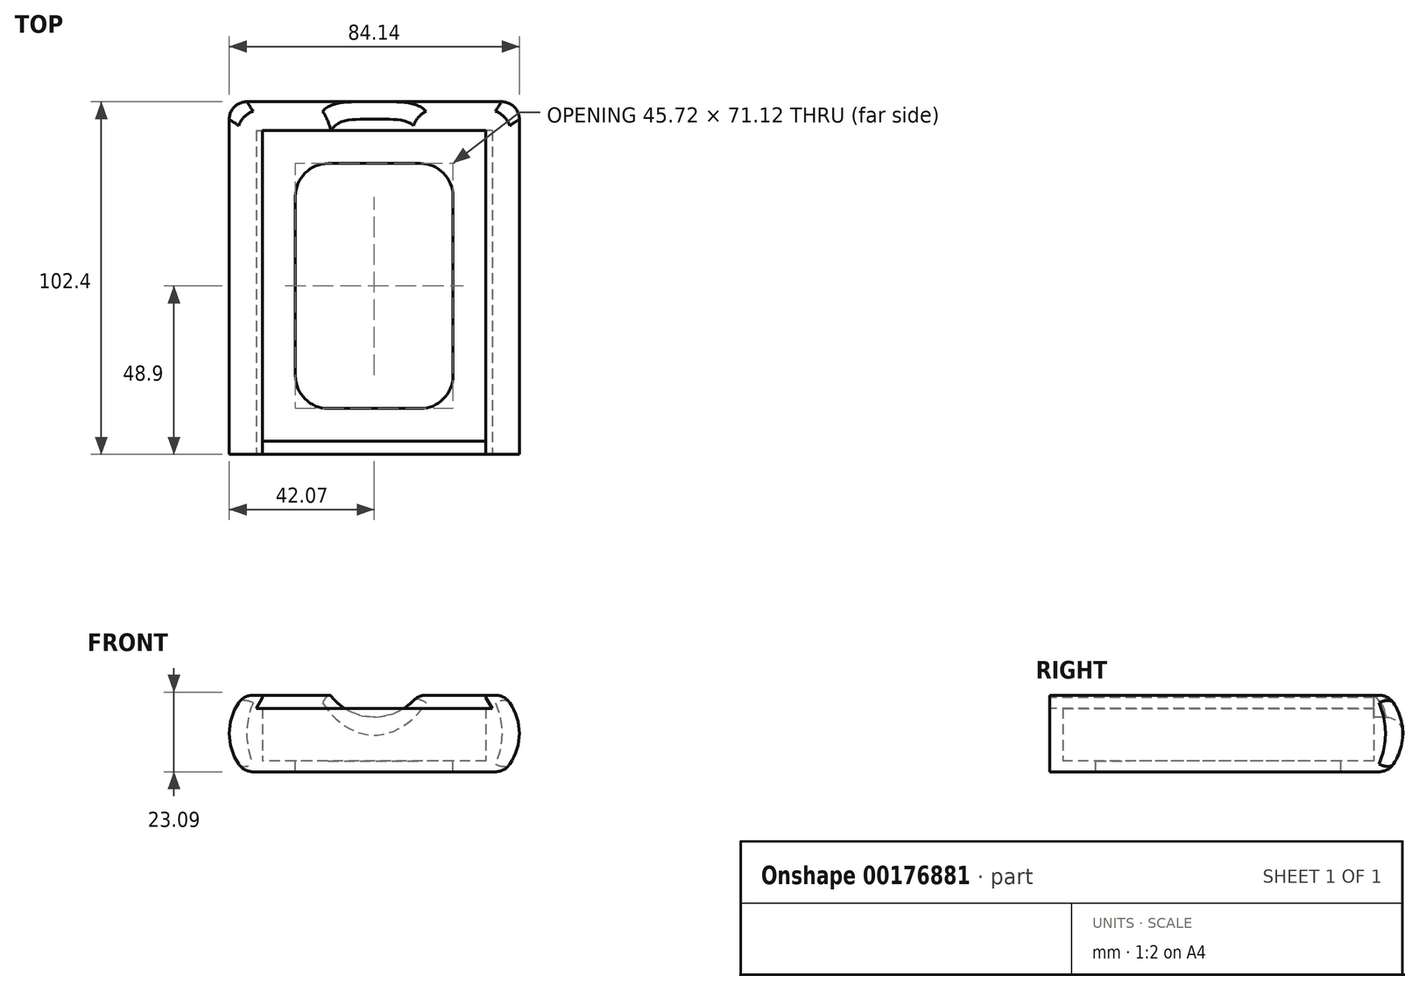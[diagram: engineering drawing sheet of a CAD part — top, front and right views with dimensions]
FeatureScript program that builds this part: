
annotation { "Feature Type Name" : "Feature", "Feature Type Description" : "" }
export const myFeature = defineFeature(function(context is Context, id is Id, definition is map)
    precondition{}
    {
        {
            var Q0;
            Q0=qCreatedBy(makeId("Top.planeOp"),FACE);
            var sketch = newSketch(context, id + "F0", { "sketchPlane" : qUnion([Q0])});
            skLineSegment(sketch, "E0.bottom", {"start": v(32.39, 45.09) * mm, "end": v(-32.39, 45.09) * mm, "construction": true});
            skLineSegment(sketch, "E0.top", {"start": v(32.39, -45.09) * mm, "end": v(-32.39, -45.09) * mm, "construction": true});
            skLineSegment(sketch, "E0.left", {"start": v(32.39, 45.09) * mm, "end": v(32.39, -45.09) * mm, "construction": true});
            skLineSegment(sketch, "E0.right", {"start": v(-32.39, 45.09) * mm, "end": v(-32.39, -45.09) * mm, "construction": true});
            skPoint(sketch, "E0.middle", {"position": v(0, 0) * mm});
            skLineSegment(sketch, "E1.bottom", {"start": v(37.47, 48.9) * mm, "end": v(-37.47, 48.9) * mm});
            skLineSegment(sketch, "E1.top", {"start": v(37.47, -48.9) * mm, "end": v(-37.47, -48.9) * mm});
            skLineSegment(sketch, "E1.left", {"start": v(37.47, 48.9) * mm, "end": v(37.47, -48.9) * mm});
            skLineSegment(sketch, "E1.right", {"start": v(-37.47, 48.9) * mm, "end": v(-37.47, -48.9) * mm});
            skSolve(sketch);
        }
        {
            var Q0;
            Q0 = qSketchRegion(id + "F0", true);
            var Q1;
            Q1=sQuery(id+"F0.wireOp",EDGE,"E0.bottom");
            var Q2;
            Q2=sQuery(id+"F0.wireOp",EDGE,"E0.right");
            var Q3;
            Q3=sQuery(id+"F0.wireOp",EDGE,"E0.top");
            var Q4;
            Q4=sQuery(id+"F0.wireOp",EDGE,"E0.left");
            extrude(context, id + "F1", {"entities" : qUnion([Q0]), "surfaceEntities" : qUnion([Q1, Q2, Q3, Q4]), "depth" : 3.17 * mm});
        }
        {
            var Q0;
            Q0=makeQuery(id+"F1.opExtrude","CAP_FACE",FACE,{"disambiguationData":[OSD([sQuery(id+"F0.wireOp",EDGE,"E1.bottom"),sQuery(id+"F0.wireOp",EDGE,"E1.top"),sQuery(id+"F0.wireOp",EDGE,"E1.left"),sQuery(id+"F0.wireOp",EDGE,"E1.right")])],"isStart":false});
            var sketch = newSketch(context, id + "F2", { "sketchPlane" : qUnion([Q0])});
            skLineSegment(sketch, "E2.bottom", {"start": v(-37.47, 48.9) * mm, "end": v(37.47, 48.9) * mm});
            skLineSegment(sketch, "E2.top", {"start": v(-37.47, -48.9) * mm, "end": v(37.47, -48.9) * mm});
            skLineSegment(sketch, "E2.left", {"start": v(-37.47, 48.9) * mm, "end": v(-37.47, -48.9) * mm});
            skLineSegment(sketch, "E2.right", {"start": v(37.47, 48.9) * mm, "end": v(37.47, -48.9) * mm});
            skLineSegment(sketch, "E3.bottom", {"start": v(32.38, 45.09) * mm, "end": v(-32.39, 45.09) * mm});
            skLineSegment(sketch, "E3.top", {"start": v(32.39, -45.09) * mm, "end": v(-32.38, -45.09) * mm});
            skLineSegment(sketch, "E3.left", {"start": v(32.38, 45.09) * mm, "end": v(32.39, -45.09) * mm});
            skLineSegment(sketch, "E3.right", {"start": v(-32.39, 45.09) * mm, "end": v(-32.38, -45.09) * mm});
            skPoint(sketch, "E3.middle", {"position": v(0, 0) * mm});
            skSolve(sketch);
        }
        {
            var Q0;
            Q0 = qSketchRegion(id + "F2", true);
            extrude(context, id + "F3", {"entities" : qUnion([Q0]), "operationType" : NewBodyOperationType.ADD, "depth" : 19.05 * mm});
        }
        {
            var Q0;
            Q0=makeQuery(id+"F3.boolean.opBoolean","MERGE",FACE,{"derivedFrom":[makeQuery(id+"F1.opExtrude","SWEPT_FACE",FACE,{"disambiguationData":[OSD([sQuery(id+"F0.wireOp",EDGE,"E1.top")])]}),makeQuery(id+"F3.opExtrude","SWEPT_FACE",FACE,{"disambiguationData":[OSD([sQuery(id+"F2.wireOp",EDGE,"E2.top")])]})]});
            var sketch = newSketch(context, id + "F4", { "sketchPlane" : qUnion([Q0])});
            skLineSegment(sketch, "E4", {"start": v(-32.38, 22.23) * mm, "end": v(-32.38, 21.59) * mm});
            skLineSegment(sketch, "E5", {"start": v(-32.38, 21.59) * mm, "end": v(-34.22, 18.41) * mm});
            skLineSegment(sketch, "E6", {"start": v(-34.22, 18.41) * mm, "end": v(0, 18.41) * mm});
            skLineSegment(sketch, "E7", {"start": v(0, 18.41) * mm, "end": v(0, 22.23) * mm, "construction": true});
            skLineSegment(sketch, "E8", {"start": v(0, 22.23) * mm, "end": v(-32.38, 22.23) * mm});
            skLineSegment(sketch, "E9.MirrorCS", {"start": v(0, 22.23) * mm, "end": v(32.38, 22.22) * mm});
            skLineSegment(sketch, "E10.MirrorCS", {"start": v(32.38, 22.23) * mm, "end": v(32.38, 21.59) * mm});
            skLineSegment(sketch, "E11.MirrorCS", {"start": v(32.38, 21.59) * mm, "end": v(34.22, 18.41) * mm});
            skLineSegment(sketch, "E12.MirrorCS", {"start": v(34.22, 18.42) * mm, "end": v(0, 18.41) * mm});
            skSolve(sketch);
        }
        {
            var Q0;
            Q0 = qSketchRegion(id + "F4", true);
            var Q1;
            Q1=makeQuery(id+"F3.opExtrude","SWEPT_FACE",FACE,{"disambiguationData":[OSD([sQuery(id+"F2.wireOp",EDGE,"E3.bottom")])]});
            extrude(context, id + "F5", {"entities" : qUnion([Q0]), "operationType" : NewBodyOperationType.REMOVE, "endBound" : BoundingType.UP_TO_SURFACE, "oppositeDirection" : true, "endBoundEntityFace" : qUnion([Q1]), "depth" : 25.4 * mm});
        }
        {
            var Q0;
            Q0=makeQuery(id+"F3.boolean.opBoolean","MERGE",FACE,{"derivedFrom":[makeQuery(id+"F1.opExtrude","SWEPT_FACE",FACE,{"disambiguationData":[OSD([sQuery(id+"F0.wireOp",EDGE,"E1.top")])]}),makeQuery(id+"F3.opExtrude","SWEPT_FACE",FACE,{"disambiguationData":[OSD([sQuery(id+"F2.wireOp",EDGE,"E2.top")])]})]});
            var sketch = newSketch(context, id + "F6", { "sketchPlane" : qUnion([Q0])});
            skArc(sketch, "E13", {"start": v(-37.47, 22.23) * mm, "mid": v(-42.07, 11.11) * mm, "end": v(-37.47, 0) * mm});
            skLineSegment(sketch, "E14", {"start": v(-37.46, 0) * mm, "end": v(-37.46, 22.23) * mm});
            skLineSegment(sketch, "E15", {"start": v(-37.47, 0) * mm, "end": v(-48.04, 10.57) * mm, "construction": true});
            skSolve(sketch);
        }
        {
            var Q0;
            Q0=qCreatedBy(makeId("Top.planeOp"),FACE);
            var sketch = newSketch(context, id + "F7", { "sketchPlane" : qUnion([Q0])});
            skLineSegment(sketch, "E16", {"start": v(-37.47, -48.9) * mm, "end": v(-37.47, 48.9) * mm});
            skLineSegment(sketch, "E17", {"start": v(-37.47, 48.9) * mm, "end": v(37.47, 48.9) * mm});
            skLineSegment(sketch, "E18", {"start": v(37.47, 48.9) * mm, "end": v(37.47, -48.9) * mm});
            skSolve(sketch);
        }
        {
            var Q0;
            Q0 = qSketchRegion(id + "F6", true);
            var Q1;
            Q1 = qConstructionFilter(qBodyType(qCreatedBy(id + "F7" ,EDGE), BodyType.WIRE), ConstructionObject.NO);
            sweep(context, id + "F8", {"operationType" : NewBodyOperationType.ADD, "profiles" : qUnion([Q0]), "path" : qUnion([Q1])});
        }
        {
            var Q0;
            {var subQ0=sQuery(id+"F2.wireOp",EDGE,"E3.bottom");Q0=makeQuery(id+"F5.boolean.opBoolean","MERGE",FACE,{"derivedFrom":[makeQuery(id+"F3.opExtrude","SWEPT_FACE",FACE,{"disambiguationData":[OSD([subQ0])]}),makeQuery(id+"F5.opExtrude","CAP_FACE",FACE,{"disambiguationData":[OSD([subQ0])],"isStart":false})]});}
            var sketch = newSketch(context, id + "F9", { "sketchPlane" : qUnion([Q0])});
            skArc(sketch, "E19", {"start": v(-12.7, 22.23) * mm, "mid": v(0, 15.87) * mm, "end": v(12.7, 22.23) * mm});
            skLineSegment(sketch, "E20", {"start": v(-12.7, 22.23) * mm, "end": v(0, 22.23) * mm});
            skLineSegment(sketch, "E21", {"start": v(0, 22.23) * mm, "end": v(12.7, 22.23) * mm});
            skLineSegment(sketch, "E22", {"start": v(0, 22.23) * mm, "end": v(0, 15.88) * mm, "construction": true});
            skSolve(sketch);
        }
        {
            var Q0;
            Q0 = qSketchRegion(id + "F9", true);
            extrude(context, id + "F10", {"entities" : qUnion([Q0]), "operationType" : NewBodyOperationType.REMOVE, "endBound" : BoundingType.THROUGH_ALL, "oppositeDirection" : true, "depth" : 25.4 * mm});
        }
        {
            var Q0;
            Q0=makeQuery(id+"F1.opExtrude","CAP_FACE",FACE,{"disambiguationData":[OSD([sQuery(id+"F0.wireOp",EDGE,"E1.bottom"),sQuery(id+"F0.wireOp",EDGE,"E1.top"),sQuery(id+"F0.wireOp",EDGE,"E1.left"),sQuery(id+"F0.wireOp",EDGE,"E1.right")])],"isStart":false});
            var sketch = newSketch(context, id + "F11", { "sketchPlane" : qUnion([Q0])});
            skLineSegment(sketch, "E23.bottom", {"start": v(-32.39, 45.09) * mm, "end": v(32.39, 45.09) * mm, "construction": true});
            skLineSegment(sketch, "E23.top", {"start": v(-32.39, -45.09) * mm, "end": v(32.39, -45.09) * mm, "construction": true});
            skLineSegment(sketch, "E23.left", {"start": v(-32.39, 45.09) * mm, "end": v(-32.39, -45.09) * mm, "construction": true});
            skLineSegment(sketch, "E23.right", {"start": v(32.39, 45.09) * mm, "end": v(32.39, -45.09) * mm, "construction": true});
            skLineSegment(sketch, "E24.bottom", {"start": v(-22.86, 35.56) * mm, "end": v(22.86, 35.56) * mm});
            skLineSegment(sketch, "E24.top", {"start": v(-22.86, -35.56) * mm, "end": v(22.86, -35.56) * mm});
            skLineSegment(sketch, "E24.left", {"start": v(-22.86, 35.56) * mm, "end": v(-22.86, -35.56) * mm});
            skLineSegment(sketch, "E24.right", {"start": v(22.86, 35.56) * mm, "end": v(22.86, -35.56) * mm});
            skPoint(sketch, "E24.middle", {"position": v(0, 0) * mm});
            skSolve(sketch);
        }
        {
            var Q0;
            Q0 = qSketchRegion(id + "F11", true);
            extrude(context, id + "F12", {"entities" : qUnion([Q0]), "operationType" : NewBodyOperationType.REMOVE, "endBound" : BoundingType.THROUGH_ALL, "oppositeDirection" : true, "depth" : 25.4 * mm});
        }
        {
            var Q0;
            Q0=makeQuery(id+"F10.boolean.opBoolean","COPY",EDGE,{"derivedFrom":makeQuery(id+"F10.opExtrude","SWEPT_EDGE",EDGE,{"disambiguationData":[OSD([sQuery(id+"F2.wireOp",EDGE,"E3.bottom"),sQuery(id+"F9.wireOp",EDGE,"E19"),sQuery(id+"F9.wireOp",EDGE,"E20")])]})});
            var Q1;
            Q1=makeQuery(id+"F10.boolean.opBoolean","INTERSECT",EDGE,{"derivedFrom":[makeQuery(id+"F8.opSweep","SWEPT_FACE",FACE,{"disambiguationData":[OSD([sQuery(id+"F6.wireOp",EDGE,"E13"),sQuery(id+"F7.wireOp",EDGE,"E17")])]}),makeQuery(id+"F10.opExtrude","SWEPT_FACE",FACE,{"disambiguationData":[OSD([sQuery(id+"F9.wireOp",EDGE,"E19")])]})]});
            var Q2;
            Q2=makeQuery(id+"F10.boolean.opBoolean","COPY",EDGE,{"derivedFrom":makeQuery(id+"F10.opExtrude","SWEPT_EDGE",EDGE,{"disambiguationData":[OSD([sQuery(id+"F2.wireOp",EDGE,"E3.bottom"),sQuery(id+"F9.wireOp",EDGE,"E19"),sQuery(id+"F9.wireOp",EDGE,"E21")])]})});
            var Q3;
            Q3=makeQuery(id+"F8.opSweep","MID_CAP_EDGE",EDGE,{"disambiguationData":[OSD([sQuery(id+"F6.wireOp",EDGE,"E13"),sQuery(id+"F7.wireOp",VERTEX,"E18.start")])],"capPos":2.0});
            var Q4;
            Q4=makeQuery(id+"F8.opSweep","MID_CAP_EDGE",EDGE,{"disambiguationData":[OSD([sQuery(id+"F6.wireOp",EDGE,"E13"),sQuery(id+"F7.wireOp",VERTEX,"E17.start")])],"capPos":1.0});
            var Q5;
            Q5=makeQuery(id+"F8.boolean.opBoolean","MERGE",EDGE,{"derivedFrom":[makeQuery(id+"F3.opExtrude","CAP_EDGE",EDGE,{"disambiguationData":[OSD([sQuery(id+"F2.wireOp",EDGE,"E2.right")])],"isStart":false}),makeQuery(id+"F8.opSweep","SWEPT_EDGE",EDGE,{"disambiguationData":[OSD([sQuery(id+"F2.wireOp",EDGE,"E2.top"),sQuery(id+"F6.wireOp",EDGE,"E13"),sQuery(id+"F6.wireOp",EDGE,"E14"),sQuery(id+"F7.wireOp",EDGE,"E18")])]})]});
            var Q6;
            {var subQ0=sQuery(id+"F2.wireOp",EDGE,"E2.top");var subQ1=sQuery(id+"F2.wireOp",EDGE,"E2.bottom");var subQ2=sQuery(id+"F7.wireOp",EDGE,"E17");var subQ3=sQuery(id+"F6.wireOp",EDGE,"E13");Q6=makeQuery(id+"F10.boolean.opBoolean","SPLIT",EDGE,{"disambiguationData":[TD([makeQuery(id+"F8.opSweep","SWEPT_FACE",FACE,{"disambiguationData":[OSD([subQ3,sQuery(id+"F7.wireOp",EDGE,"E18")])]})])],"derivedFrom":makeQuery(id+"F8.boolean.opBoolean","MERGE",EDGE,{"derivedFrom":[makeQuery(id+"F3.opExtrude","CAP_EDGE",EDGE,{"disambiguationData":[OSD([subQ1])],"isStart":false}),makeQuery(id+"F8.opSweep","SWEPT_EDGE",EDGE,{"disambiguationData":[OSD([subQ0,subQ3,sQuery(id+"F6.wireOp",EDGE,"E14"),subQ2])]})]})});}
            var Q7;
            {var subQ0=sQuery(id+"F2.wireOp",EDGE,"E2.top");var subQ1=sQuery(id+"F2.wireOp",EDGE,"E2.bottom");var subQ2=sQuery(id+"F6.wireOp",EDGE,"E13");var subQ3=sQuery(id+"F7.wireOp",EDGE,"E17");Q7=makeQuery(id+"F10.boolean.opBoolean","SPLIT",EDGE,{"disambiguationData":[TD([makeQuery(id+"F8.opSweep","SWEPT_FACE",FACE,{"disambiguationData":[OSD([subQ2,sQuery(id+"F7.wireOp",EDGE,"E16")])]})])],"derivedFrom":makeQuery(id+"F8.boolean.opBoolean","MERGE",EDGE,{"derivedFrom":[makeQuery(id+"F3.opExtrude","CAP_EDGE",EDGE,{"disambiguationData":[OSD([subQ1])],"isStart":false}),makeQuery(id+"F8.opSweep","SWEPT_EDGE",EDGE,{"disambiguationData":[OSD([subQ0,subQ2,sQuery(id+"F6.wireOp",EDGE,"E14"),subQ3])]})]})});}
            var Q8;
            Q8=makeQuery(id+"F8.boolean.opBoolean","MERGE",EDGE,{"derivedFrom":[makeQuery(id+"F3.opExtrude","CAP_EDGE",EDGE,{"disambiguationData":[OSD([sQuery(id+"F2.wireOp",EDGE,"E2.left")])],"isStart":false}),makeQuery(id+"F8.opSweep","SWEPT_EDGE",EDGE,{"disambiguationData":[OSD([sQuery(id+"F2.wireOp",EDGE,"E2.top"),sQuery(id+"F6.wireOp",EDGE,"E13"),sQuery(id+"F6.wireOp",EDGE,"E14"),sQuery(id+"F7.wireOp",EDGE,"E16")])]})]});
            var Q9;
            Q9=makeQuery(id+"F8.boolean.opBoolean","MERGE",EDGE,{"derivedFrom":[makeQuery(id+"F1.opExtrude","CAP_EDGE",EDGE,{"disambiguationData":[OSD([sQuery(id+"F0.wireOp",EDGE,"E1.bottom")])],"isStart":true}),makeQuery(id+"F8.opSweep","SWEPT_EDGE",EDGE,{"disambiguationData":[OSD([sQuery(id+"F0.wireOp",EDGE,"E1.top"),sQuery(id+"F6.wireOp",EDGE,"E13"),sQuery(id+"F6.wireOp",EDGE,"E14"),sQuery(id+"F7.wireOp",EDGE,"E17")])]})]});
            var Q10;
            Q10=makeQuery(id+"F8.boolean.opBoolean","MERGE",EDGE,{"derivedFrom":[makeQuery(id+"F1.opExtrude","CAP_EDGE",EDGE,{"disambiguationData":[OSD([sQuery(id+"F0.wireOp",EDGE,"E1.right")])],"isStart":true}),makeQuery(id+"F8.opSweep","SWEPT_EDGE",EDGE,{"disambiguationData":[OSD([sQuery(id+"F0.wireOp",EDGE,"E1.top"),sQuery(id+"F6.wireOp",EDGE,"E13"),sQuery(id+"F6.wireOp",EDGE,"E14"),sQuery(id+"F7.wireOp",EDGE,"E16")])]})]});
            var Q11;
            Q11=makeQuery(id+"F8.boolean.opBoolean","MERGE",EDGE,{"derivedFrom":[makeQuery(id+"F1.opExtrude","CAP_EDGE",EDGE,{"disambiguationData":[OSD([sQuery(id+"F0.wireOp",EDGE,"E1.left")])],"isStart":true}),makeQuery(id+"F8.opSweep","SWEPT_EDGE",EDGE,{"disambiguationData":[OSD([sQuery(id+"F0.wireOp",EDGE,"E1.top"),sQuery(id+"F6.wireOp",EDGE,"E13"),sQuery(id+"F6.wireOp",EDGE,"E14"),sQuery(id+"F7.wireOp",EDGE,"E18")])]})]});
            fillet(context, id + "F13", {"entities" : qUnion([Q0, Q1, Q2, Q3, Q4, Q5, Q6, Q7, Q8, Q9, Q10, Q11]), "radius" : 5.08 * mm, "tangentPropagation" : true, "allowEdgeOverflow" : false});
        }
        {
            var Q0;
            Q0=makeQuery(id+"F12.boolean.opBoolean","COPY",EDGE,{"derivedFrom":makeQuery(id+"F12.opExtrude","SWEPT_EDGE",EDGE,{"disambiguationData":[OSD([sQuery(id+"F11.wireOp",EDGE,"E24.bottom"),sQuery(id+"F11.wireOp",EDGE,"E24.right")])]})});
            var Q1;
            Q1=makeQuery(id+"F12.boolean.opBoolean","COPY",EDGE,{"derivedFrom":makeQuery(id+"F12.opExtrude","SWEPT_EDGE",EDGE,{"disambiguationData":[OSD([sQuery(id+"F11.wireOp",EDGE,"E24.bottom"),sQuery(id+"F11.wireOp",EDGE,"E24.left")])]})});
            var Q2;
            Q2=makeQuery(id+"F12.boolean.opBoolean","COPY",EDGE,{"derivedFrom":makeQuery(id+"F12.opExtrude","SWEPT_EDGE",EDGE,{"disambiguationData":[OSD([sQuery(id+"F11.wireOp",EDGE,"E24.top"),sQuery(id+"F11.wireOp",EDGE,"E24.left")])]})});
            var Q3;
            Q3=makeQuery(id+"F12.boolean.opBoolean","COPY",EDGE,{"derivedFrom":makeQuery(id+"F12.opExtrude","SWEPT_EDGE",EDGE,{"disambiguationData":[OSD([sQuery(id+"F11.wireOp",EDGE,"E24.top"),sQuery(id+"F11.wireOp",EDGE,"E24.right")])]})});
            fillet(context, id + "F14", {"entities" : qUnion([Q0, Q1, Q2, Q3]), "radius" : 9.52 * mm, "tangentPropagation" : true, "allowEdgeOverflow" : false});
        }
    });
